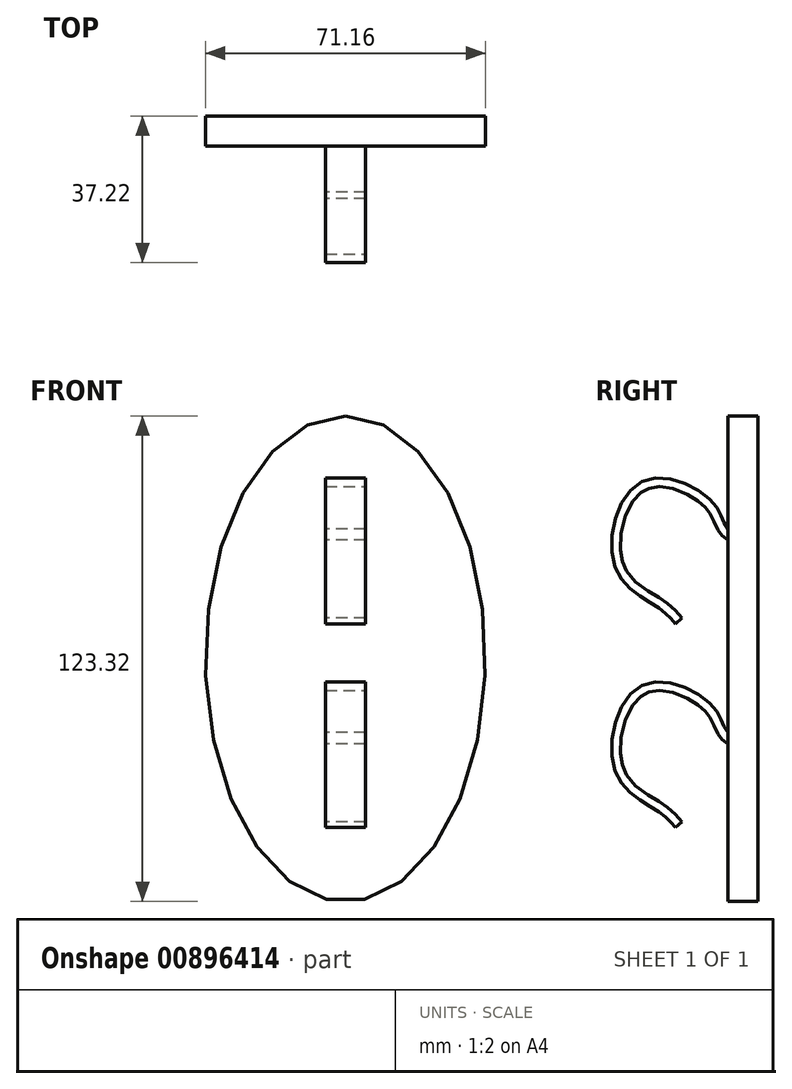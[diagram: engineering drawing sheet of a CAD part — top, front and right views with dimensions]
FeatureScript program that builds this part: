
annotation { "Feature Type Name" : "Feature", "Feature Type Description" : "" }
export const myFeature = defineFeature(function(context is Context, id is Id, definition is map)
    precondition{}
    {
        {
            var Q0;
            Q0=qCreatedBy(makeId("Front.planeOp"),FACE);
            var sketch = newSketch(context, id + "F0", { "sketchPlane" : qUnion([Q0])});
            skEllipse(sketch, "E0", {"center": v(0, 0) * mm, "majorRadius": 61.66 * mm, "minorRadius": 35.58 * mm, "majorAxis": v(0, 1)});
            skSolve(sketch);
        }
        {
            var Q0;
            Q0 = qSketchRegion(id + "F0", true);
            extrude(context, id + "F1", {"entities" : qUnion([Q0]), "depth" : 7.62 * mm, "offsetDistance" : 25.4 * mm});
        }
        {
            var Q0;
            Q0=qCreatedBy(makeId("Right.planeOp"),FACE);
            var sketch = newSketch(context, id + "F2", { "sketchPlane" : qUnion([Q0])});
            skFitSpline(sketch, "E1", {"points": [v(-0.06, -22.6) * mm, v(-7.72, -18.67) * mm, v(-11.26, -12.29) * mm, v(-29.4, -6.76) * mm, v(-36.33, -28.54) * mm, v(-25.41, -38.74) * mm, v(-21, -42.9) * mm], "startDerivative": vector(-65.32, 29.05) * mm, "endDerivative": vector(29.8, -35.25) * mm});
            skFitSpline(sketch, "E2.0", {"points": [v(-0.98, -24.67) * mm, v(-1.61, -24.39) * mm, v(-2.93, -23.85) * mm, v(-4.6, -23.19) * mm, v(-5.92, -22.6) * mm, v(-6.88, -22.12) * mm, v(-7.66, -21.66) * mm, v(-8.25, -21.24) * mm, v(-8.69, -20.89) * mm, v(-9.04, -20.57) * mm, v(-9.3, -20.3) * mm, v(-9.56, -20) * mm, v(-9.85, -19.63) * mm, v(-10.25, -19.03) * mm, v(-10.64, -18.28) * mm, v(-11, -17.44) * mm, v(-11.31, -16.66) * mm, v(-11.62, -15.92) * mm, v(-11.97, -15.22) * mm, v(-12.3, -14.65) * mm, v(-12.64, -14.18) * mm, v(-12.91, -13.83) * mm, v(-13.23, -13.47) * mm, v(-13.73, -12.97) * mm, v(-14.46, -12.31) * mm, v(-15.48, -11.53) * mm, v(-16.64, -10.78) * mm, v(-18.3, -9.85) * mm, v(-20.57, -8.87) * mm, v(-22.89, -8.28) * mm, v(-24.66, -8.1) * mm, v(-25.91, -8.12) * mm, v(-27.08, -8.3) * mm, v(-27.96, -8.58) * mm, v(-28.6, -8.88) * mm, v(-29.25, -9.25) * mm, v(-30.03, -9.84) * mm, v(-30.94, -10.75) * mm, v(-32.06, -12.2) * mm, v(-33.28, -14.44) * mm, v(-34.34, -17.53) * mm, v(-34.93, -20.8) * mm, v(-35, -23.47) * mm, v(-34.8, -25.44) * mm, v(-34.57, -26.58) * mm, v(-34.33, -27.4) * mm, v(-34.06, -28.18) * mm, v(-33.47, -29.44) * mm, v(-32.35, -31) * mm, v(-30.64, -32.63) * mm, v(-28.68, -34.05) * mm, v(-26.97, -35.1) * mm, v(-25.62, -35.92) * mm, v(-24.64, -36.53) * mm, v(-23.7, -37.17) * mm, v(-22.86, -37.8) * mm, v(-22.1, -38.44) * mm, v(-21.2, -39.28) * mm, v(-20.24, -40.3) * mm, v(-19.6, -41.07) * mm, v(-19.28, -41.44) * mm]});
            skLineSegment(sketch, "E3", {"start": v(-21, -42.9) * mm, "end": v(-19.28, -41.44) * mm});
            skLineSegment(sketch, "E4", {"start": v(-0.98, -24.67) * mm, "end": v(-0.06, -22.6) * mm});
            skFitSpline(sketch, "E5", {"points": [v(-0.06, 29.2) * mm, v(-7.72, 33.13) * mm, v(-11.26, 39.5) * mm, v(-29.4, 45.04) * mm, v(-36.33, 23.26) * mm, v(-25.41, 13.06) * mm, v(-21, 8.9) * mm], "startDerivative": vector(-65.32, 29.05) * mm, "endDerivative": vector(29.8, -35.25) * mm});
            skFitSpline(sketch, "E6.0", {"points": [v(-0.98, 27.13) * mm, v(-1.61, 27.4) * mm, v(-2.93, 27.94) * mm, v(-4.6, 28.6) * mm, v(-5.92, 29.2) * mm, v(-6.88, 29.67) * mm, v(-7.66, 30.14) * mm, v(-8.25, 30.56) * mm, v(-8.69, 30.9) * mm, v(-9.04, 31.23) * mm, v(-9.3, 31.5) * mm, v(-9.56, 31.8) * mm, v(-9.85, 32.17) * mm, v(-10.25, 32.77) * mm, v(-10.64, 33.51) * mm, v(-11, 34.35) * mm, v(-11.31, 35.14) * mm, v(-11.62, 35.87) * mm, v(-11.97, 36.58) * mm, v(-12.3, 37.15) * mm, v(-12.64, 37.62) * mm, v(-12.91, 37.97) * mm, v(-13.23, 38.33) * mm, v(-13.73, 38.83) * mm, v(-14.46, 39.48) * mm, v(-15.48, 40.27) * mm, v(-16.64, 41.02) * mm, v(-18.3, 41.95) * mm, v(-20.57, 42.93) * mm, v(-22.89, 43.52) * mm, v(-24.66, 43.7) * mm, v(-25.91, 43.68) * mm, v(-27.08, 43.5) * mm, v(-27.96, 43.22) * mm, v(-28.6, 42.92) * mm, v(-29.25, 42.55) * mm, v(-30.03, 41.95) * mm, v(-30.94, 41.05) * mm, v(-32.06, 39.59) * mm, v(-33.28, 37.36) * mm, v(-34.34, 34.26) * mm, v(-34.93, 31) * mm, v(-35, 28.32) * mm, v(-34.8, 26.35) * mm, v(-34.57, 25.22) * mm, v(-34.33, 24.39) * mm, v(-34.06, 23.61) * mm, v(-33.47, 22.36) * mm, v(-32.35, 20.8) * mm, v(-30.64, 19.17) * mm, v(-28.68, 17.75) * mm, v(-26.97, 16.69) * mm, v(-25.62, 15.87) * mm, v(-24.64, 15.26) * mm, v(-23.7, 14.63) * mm, v(-22.86, 14) * mm, v(-22.1, 13.36) * mm, v(-21.2, 12.51) * mm, v(-20.24, 11.5) * mm, v(-19.6, 10.72) * mm, v(-19.28, 10.36) * mm]});
            skLineSegment(sketch, "E7", {"start": v(-21, 8.9) * mm, "end": v(-19.28, 10.36) * mm});
            skLineSegment(sketch, "E8", {"start": v(-0.98, 27.13) * mm, "end": v(-0.06, 29.2) * mm});
            skSolve(sketch);
        }
        {
            var Q0;
            Q0 = qSketchRegion(id + "F2", true);
            extrude(context, id + "F3", {"entities" : qUnion([Q0]), "operationType" : NewBodyOperationType.ADD, "endBound" : BoundingType.SYMMETRIC, "depth" : 10.26 * mm, "offsetDistance" : 25.4 * mm});
        }
    });
